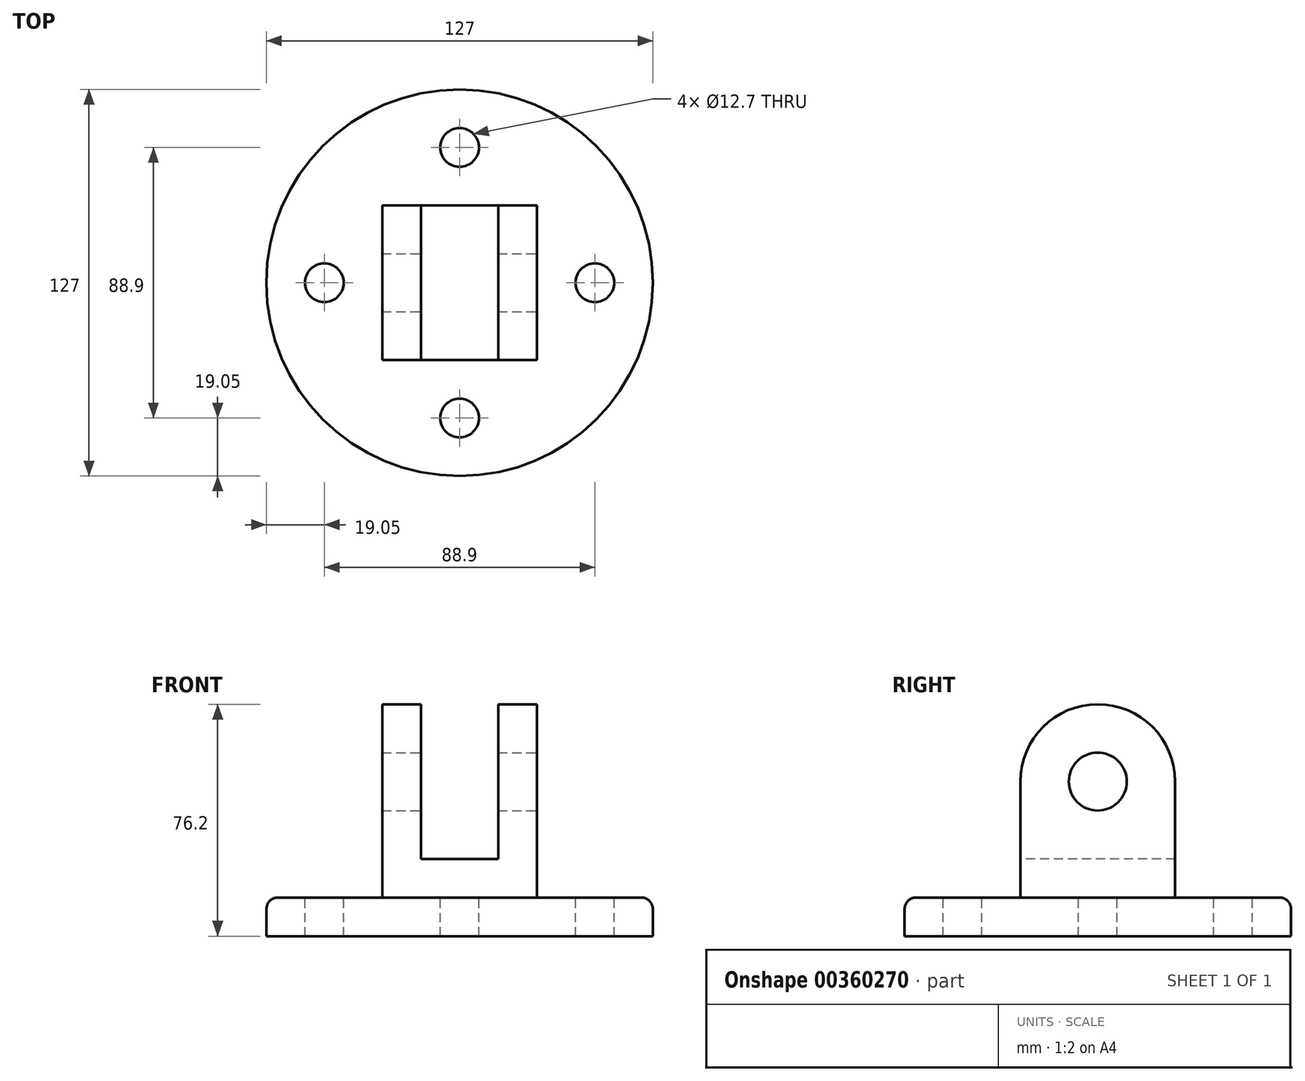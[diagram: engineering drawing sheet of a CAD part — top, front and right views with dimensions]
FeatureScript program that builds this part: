
annotation { "Feature Type Name" : "Feature", "Feature Type Description" : "" }
export const myFeature = defineFeature(function(context is Context, id is Id, definition is map)
    precondition{}
    {
        {
            var Q0;
            Q0=qCreatedBy(makeId("Top.planeOp"),FACE);
            var sketch = newSketch(context, id + "F0", { "sketchPlane" : qUnion([Q0])});
            skCircle(sketch, "E0", {"center": v(0, 0) * mm, "radius": 63.5 * mm});
            skCircle(sketch, "E1", {"center": v(0, 0) * mm, "radius": 44.45 * mm, "construction": true});
            skLineSegment(sketch, "E2.bottom", {"start": v(-25.4, 25.4) * mm, "end": v(25.4, 25.4) * mm});
            skLineSegment(sketch, "E2.top", {"start": v(-25.4, -25.4) * mm, "end": v(25.4, -25.4) * mm});
            skLineSegment(sketch, "E2.left", {"start": v(-25.4, 25.4) * mm, "end": v(-25.4, -25.4) * mm});
            skLineSegment(sketch, "E2.right", {"start": v(25.4, 25.4) * mm, "end": v(25.4, -25.4) * mm});
            skLineSegment(sketch, "E3", {"start": v(0, 0) * mm, "end": v(0, 25.4) * mm, "construction": true});
            skLineSegment(sketch, "E4", {"start": v(0, 0) * mm, "end": v(0, -25.4) * mm, "construction": true});
            skLineSegment(sketch, "E5", {"start": v(0, 0) * mm, "end": v(25.4, 0) * mm, "construction": true});
            skLineSegment(sketch, "E6", {"start": v(0, 0) * mm, "end": v(-25.4, 0) * mm, "construction": true});
            skLineSegment(sketch, "E7", {"start": v(25.4, 0) * mm, "end": v(63.5, 0) * mm, "construction": true});
            skLineSegment(sketch, "E8", {"start": v(0, 25.4) * mm, "end": v(0, 63.5) * mm, "construction": true});
            skLineSegment(sketch, "E9", {"start": v(-25.4, 0) * mm, "end": v(-63.5, 0) * mm, "construction": true});
            skLineSegment(sketch, "E10", {"start": v(0, -25.4) * mm, "end": v(0, -63.5) * mm, "construction": true});
            skPoint(sketch, "E11", {"position": v(0, 44.45) * mm});
            skPoint(sketch, "E12", {"position": v(44.45, 0) * mm});
            skPoint(sketch, "E13", {"position": v(0, -44.45) * mm});
            skPoint(sketch, "E14", {"position": v(-44.45, 0) * mm});
            skCircle(sketch, "E15", {"center": v(0, -44.45) * mm, "radius": 6.35 * mm});
            skCircle(sketch, "E16", {"center": v(44.45, 0) * mm, "radius": 6.35 * mm});
            skCircle(sketch, "E17", {"center": v(0, 44.45) * mm, "radius": 6.35 * mm});
            skCircle(sketch, "E18", {"center": v(-44.45, 0) * mm, "radius": 6.35 * mm});
            skLineSegment(sketch, "E19", {"start": v(-12.7, 25.4) * mm, "end": v(-12.7, -25.4) * mm});
            skLineSegment(sketch, "E20", {"start": v(12.7, -25.4) * mm, "end": v(12.7, 25.4) * mm});
            skSolve(sketch);
        }
        {
            var Q0;
            Q0=makeQuery(id+"F0.imprint","IMPRINT",FACE,{"disambiguationData":[TD([[makeQuery(id+"F0.imprint","IMPRINT",EDGE,{"derivedFrom":sQuery(id+"F0.wireOp",EDGE,"E0")}),1.0]])]});
            var Q1;
            {var subQ0=sQuery(id+"F0.wireOp",EDGE,"E2.left");Q1=makeQuery(id+"F0.imprint","IMPRINT",FACE,{"disambiguationData":[TD([[makeQuery(id+"F0.imprint","IMPRINT",EDGE,{"derivedFrom":subQ0}),1.0]])]});}
            var Q2;
            {var subQ0=sQuery(id+"F0.wireOp",EDGE,"E19");Q2=makeQuery(id+"F0.imprint","IMPRINT",FACE,{"disambiguationData":[TD([[makeQuery(id+"F0.imprint","IMPRINT",EDGE,{"derivedFrom":subQ0}),1.0]])]});}
            var Q3;
            {var subQ0=sQuery(id+"F0.wireOp",EDGE,"E2.right");Q3=makeQuery(id+"F0.imprint","IMPRINT",FACE,{"disambiguationData":[TD([[makeQuery(id+"F0.imprint","IMPRINT",EDGE,{"derivedFrom":subQ0}),-1.0]])]});}
            extrude(context, id + "F1", {"entities" : qUnion([Q0, Q1, Q2, Q3]), "oppositeDirection" : true, "depth" : 12.7 * mm});
        }
        {
            var Q0;
            {var subQ0=sQuery(id+"F0.wireOp",EDGE,"E2.left");Q0=makeQuery(id+"F0.imprint","IMPRINT",FACE,{"disambiguationData":[TD([[makeQuery(id+"F0.imprint","IMPRINT",EDGE,{"derivedFrom":subQ0}),1.0]])]});}
            var Q1;
            {var subQ0=sQuery(id+"F0.wireOp",EDGE,"E2.right");Q1=makeQuery(id+"F0.imprint","IMPRINT",FACE,{"disambiguationData":[TD([[makeQuery(id+"F0.imprint","IMPRINT",EDGE,{"derivedFrom":subQ0}),-1.0]])]});}
            extrude(context, id + "F2", {"entities" : qUnion([Q0, Q1]), "operationType" : NewBodyOperationType.ADD, "depth" : 63.5 * mm});
        }
        {
            var Q0;
            {var subQ0=sQuery(id+"F0.wireOp",EDGE,"E19");Q0=makeQuery(id+"F0.imprint","IMPRINT",FACE,{"disambiguationData":[TD([[makeQuery(id+"F0.imprint","IMPRINT",EDGE,{"derivedFrom":subQ0}),1.0]])]});}
            extrude(context, id + "F3", {"entities" : qUnion([Q0]), "operationType" : NewBodyOperationType.ADD, "depth" : 12.7 * mm});
        }
        {
            var Q0;
            Q0=makeQuery(id+"F2.opExtrude","SWEPT_FACE",FACE,{"disambiguationData":[OSD([sQuery(id+"F0.wireOp",EDGE,"E2.right")])]});
            var sketch = newSketch(context, id + "F4", { "sketchPlane" : qUnion([Q0])});
            skLineSegment(sketch, "E21.0.0", {"start": v(-25.4, 0) * mm, "end": v(25.4, 0) * mm});
            skLineSegment(sketch, "E21.0.1", {"start": v(25.4, 0) * mm, "end": v(25.4, 63.5) * mm});
            skLineSegment(sketch, "E21.0.2", {"start": v(25.4, 63.5) * mm, "end": v(-25.4, 63.5) * mm});
            skLineSegment(sketch, "E21.0.3", {"start": v(-25.4, 63.5) * mm, "end": v(-25.4, 0) * mm});
            skLineSegment(sketch, "E22", {"start": v(0, 0) * mm, "end": v(0, 63.5) * mm, "construction": true});
            skLineSegment(sketch, "E23", {"start": v(-25.4, 38.1) * mm, "end": v(25.4, 38.1) * mm, "construction": true});
            skLineSegment(sketch, "E24", {"start": v(63.5, 0) * mm, "end": v(63.5, -12.7) * mm});
            skLineSegment(sketch, "E25", {"start": v(-63.5, -12.7) * mm, "end": v(-63.5, 0) * mm});
            skPoint(sketch, "E26", {"position": v(0, 38.1) * mm});
            skCircle(sketch, "E27", {"center": v(0, 38.1) * mm, "radius": 9.53 * mm});
            skArc(sketch, "E28", {"start": v(25.4, 38.1) * mm, "mid": v(0, 63.5) * mm, "end": v(-25.4, 38.1) * mm});
            skSolve(sketch);
        }
        {
            var Q0;
            {var subQ0=sQuery(id+"F4.wireOp",EDGE,"E21.0.3");var subQ1=sQuery(id+"F4.wireOp",EDGE,"E21.0.2");var subQ2=makeQuery(id+"F4.imprint","INTERSECT",VERTEX,{"derivedFrom":[subQ1,subQ0]});Q0=makeQuery(id+"F4.imprint","IMPRINT",FACE,{"disambiguationData":[TD([[makeQuery(id+"F4.imprint","IMPRINT",EDGE,{"disambiguationData":[TD([[subQ2,1.0]])],"derivedFrom":subQ1}),1.0]])]});}
            var Q1;
            {var subQ0=sQuery(id+"F4.wireOp",EDGE,"E21.0.2");var subQ1=sQuery(id+"F4.wireOp",EDGE,"E21.0.1");var subQ2=makeQuery(id+"F4.imprint","INTERSECT",VERTEX,{"derivedFrom":[subQ1,subQ0]});Q1=makeQuery(id+"F4.imprint","IMPRINT",FACE,{"disambiguationData":[TD([[makeQuery(id+"F4.imprint","IMPRINT",EDGE,{"disambiguationData":[TD([[subQ2,-1.0]])],"derivedFrom":subQ1}),-1.0]])]});}
            extrude(context, id + "F5", {"entities" : qUnion([Q0, Q1]), "operationType" : NewBodyOperationType.REMOVE, "endBound" : BoundingType.THROUGH_ALL, "oppositeDirection" : true, "depth" : 25.4 * mm});
        }
        {
            var Q0;
            Q0=makeQuery(id+"F4.imprint","IMPRINT",FACE,{"disambiguationData":[TD([[makeQuery(id+"F4.imprint","IMPRINT",EDGE,{"derivedFrom":sQuery(id+"F4.wireOp",EDGE,"E27")}),1.0]])]});
            extrude(context, id + "F6", {"entities" : qUnion([Q0]), "operationType" : NewBodyOperationType.REMOVE, "endBound" : BoundingType.THROUGH_ALL, "oppositeDirection" : true, "depth" : 25.4 * mm});
        }
        {
            var Q0;
            Q0=makeQuery(id+"F2.opExtrude","CAP_EDGE",EDGE,{"disambiguationData":[OSD([sQuery(id+"F0.wireOp",EDGE,"E2.right")])],"isStart":true});
            var Q1;
            {var subQ0=sQuery(id+"F0.wireOp",EDGE,"E2.top");Q1=makeQuery(id+"F3.boolean.opBoolean","MERGE",EDGE,{"derivedFrom":[makeQuery(id+"F2.opExtrude","CAP_EDGE",EDGE,{"disambiguationData":[OSD([subQ0]),TDD([makeQuery(id+"F0.imprint","IMPRINT",EDGE,{"disambiguationData":[TD([[makeQuery(id+"F0.imprint","INTERSECT",VERTEX,{"derivedFrom":[subQ0,sQuery(id+"F0.wireOp",EDGE,"E2.left")]}),-1.0]])],"derivedFrom":subQ0})])],"isStart":true}),makeQuery(id+"F2.opExtrude","CAP_EDGE",EDGE,{"disambiguationData":[OSD([subQ0]),TDD([makeQuery(id+"F0.imprint","IMPRINT",EDGE,{"disambiguationData":[TD([[makeQuery(id+"F0.imprint","INTERSECT",VERTEX,{"derivedFrom":[subQ0,sQuery(id+"F0.wireOp",EDGE,"E2.right")]}),1.0]])],"derivedFrom":subQ0})])],"isStart":true}),makeQuery(id+"F3.opExtrude","CAP_EDGE",EDGE,{"disambiguationData":[OSD([subQ0])],"isStart":true})]});}
            var Q2;
            Q2=makeQuery(id+"F2.opExtrude","CAP_EDGE",EDGE,{"disambiguationData":[OSD([sQuery(id+"F0.wireOp",EDGE,"E2.left")])],"isStart":true});
            var Q3;
            {var subQ0=sQuery(id+"F0.wireOp",EDGE,"E2.bottom");Q3=makeQuery(id+"F3.boolean.opBoolean","MERGE",EDGE,{"derivedFrom":[makeQuery(id+"F2.opExtrude","CAP_EDGE",EDGE,{"disambiguationData":[OSD([subQ0]),TDD([makeQuery(id+"F0.imprint","IMPRINT",EDGE,{"disambiguationData":[TD([[makeQuery(id+"F0.imprint","INTERSECT",VERTEX,{"derivedFrom":[subQ0,sQuery(id+"F0.wireOp",EDGE,"E2.left")]}),-1.0]])],"derivedFrom":subQ0})])],"isStart":true}),makeQuery(id+"F2.opExtrude","CAP_EDGE",EDGE,{"disambiguationData":[OSD([subQ0]),TDD([makeQuery(id+"F0.imprint","IMPRINT",EDGE,{"disambiguationData":[TD([[makeQuery(id+"F0.imprint","INTERSECT",VERTEX,{"derivedFrom":[subQ0,sQuery(id+"F0.wireOp",EDGE,"E2.right")]}),1.0]])],"derivedFrom":subQ0})])],"isStart":true}),makeQuery(id+"F3.opExtrude","CAP_EDGE",EDGE,{"disambiguationData":[OSD([subQ0])],"isStart":true})]});}
            var Q4;
            Q4=makeQuery(id+"F1.opExtrude","CAP_EDGE",EDGE,{"disambiguationData":[OSD([sQuery(id+"F0.wireOp",EDGE,"E0")])],"isStart":true});
            fillet(context, id + "F7", {"entities" : qUnion([Q0, Q1, Q2, Q3, Q4]), "radius" : 3.8 * mm, "tangentPropagation" : true, "allowEdgeOverflow" : false});
        }
    });
